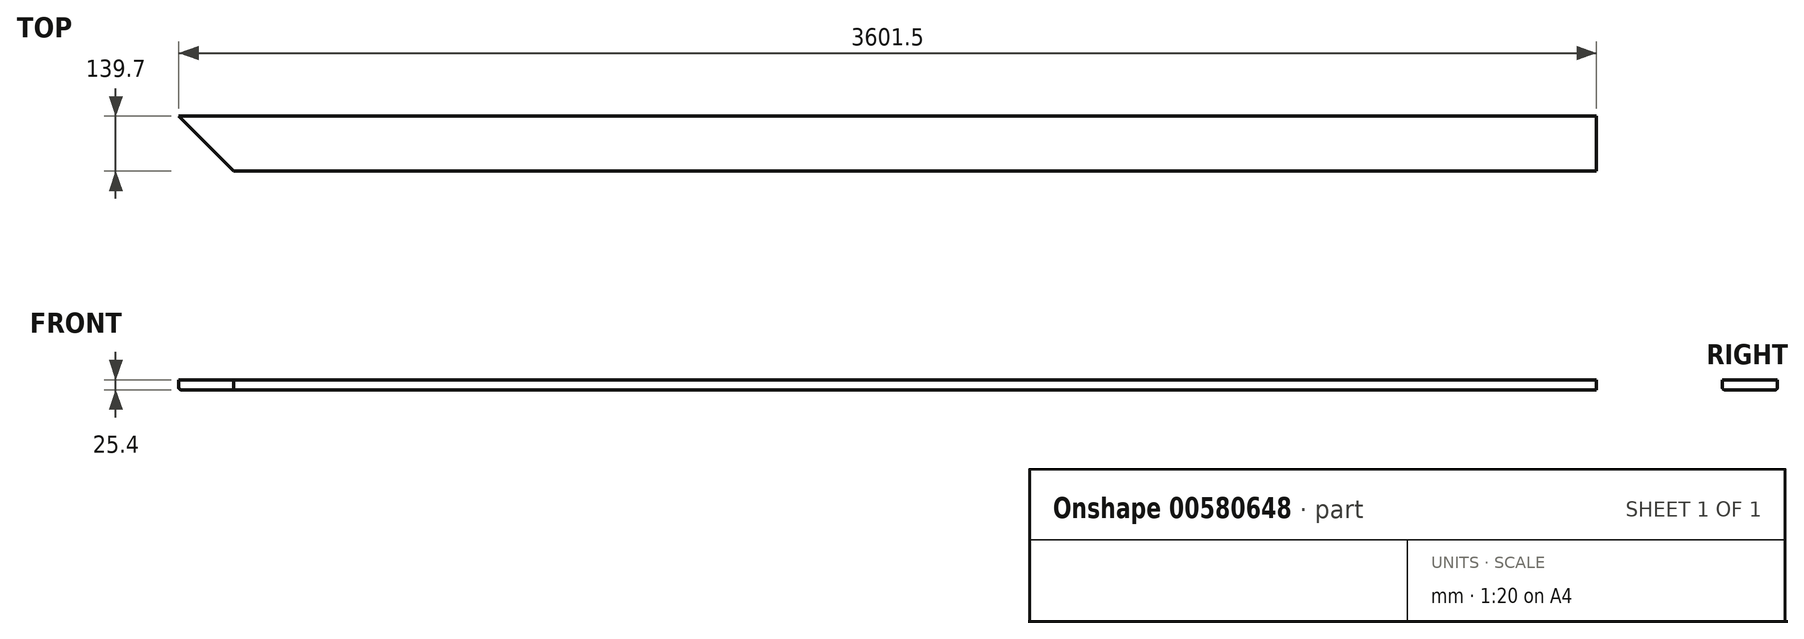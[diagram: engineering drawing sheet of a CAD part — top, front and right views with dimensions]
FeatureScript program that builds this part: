
annotation { "Feature Type Name" : "Feature", "Feature Type Description" : "" }
export const myFeature = defineFeature(function(context is Context, id is Id, definition is map)
    precondition{}
    {
        {
            var Q0;
            Q0=qCreatedBy(makeId("Top.planeOp"),FACE);
            var sketch = newSketch(context, id + "F0", { "sketchPlane" : qUnion([Q0])});
            skLineSegment(sketch, "E0.bottom", {"start": v(1800.75, -69.85) * mm, "end": v(-1661.05, -69.85) * mm});
            skLineSegment(sketch, "E0.top", {"start": v(1800.75, 69.85) * mm, "end": v(-1800.75, 69.85) * mm});
            skLineSegment(sketch, "E0.left", {"start": v(1800.75, -69.85) * mm, "end": v(1800.75, 69.85) * mm});
            skPoint(sketch, "E0.middle", {"position": v(0, 0) * mm});
            skLineSegment(sketch, "E1", {"start": v(-1800.75, 69.85) * mm, "end": v(-1661.05, -69.85) * mm});
            skSolve(sketch);
        }
        {
            var Q0;
            Q0=makeQuery(id+"F0.imprint","IMPRINT",FACE,{"disambiguationData":[TD([[makeQuery(id+"F0.imprint","IMPRINT",EDGE,{"derivedFrom":sQuery(id+"F0.wireOp",EDGE,"E0.bottom")}),-1.0]])]});
            extrude(context, id + "F1", {"entities" : qUnion([Q0]), "depth" : 25.4 * mm, "offsetDistance" : 25.4 * mm});
        }
        {
            var Q0;
            Q0=makeQuery(id+"F1.opExtrude","CAP_EDGE",EDGE,{"disambiguationData":[OSD([sQuery(id+"F0.wireOp",EDGE,"E0.bottom")])],"isStart":true});
            var Q1;
            Q1=makeQuery(id+"F1.opExtrude","CAP_EDGE",EDGE,{"disambiguationData":[OSD([sQuery(id+"F0.wireOp",EDGE,"E0.top")])],"isStart":true});
            fillet(context, id + "F2", {"entities" : qUnion([Q0, Q1]), "radius" : 5.08 * mm, "tangentPropagation" : true, "allowEdgeOverflow" : false});
        }
    });
